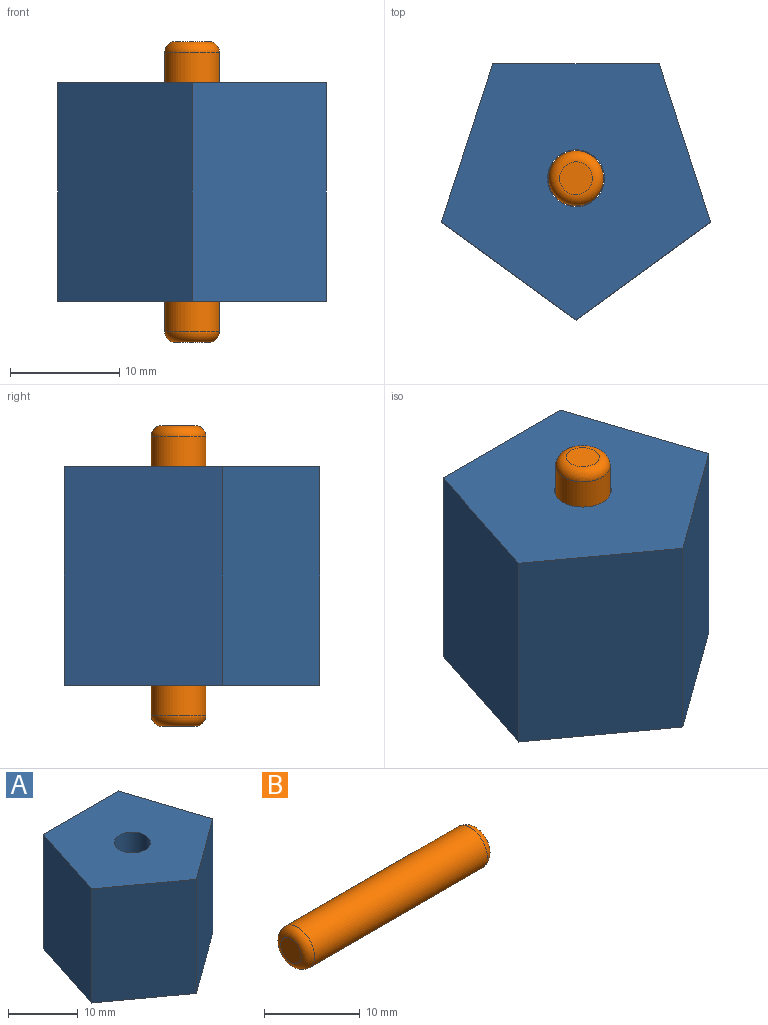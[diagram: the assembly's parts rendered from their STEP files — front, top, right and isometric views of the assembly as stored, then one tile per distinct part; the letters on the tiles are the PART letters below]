
ASSEMBLY  parts=2 mates=1
PART A: 8 faces, bbox 24.6x23.4x20 mm
  f0: plane 20x12.29mm, normal (0.59,-0.81,0), area 303.9mm2, adj f1,f5,f6,f7
  f1: plane 20x14.45mm, normal (0.95,0.31,0), area 303.9mm2, adj f0,f2,f6,f7
  f2: plane 20x15.19mm, normal (0,1,0), area 303.9mm2, adj f1,f3,f6,f7
  f3: plane 20x14.45mm, normal (-0.95,0.31,0), area 303.9mm2, adj f2,f5,f6,f7
  f4: cylinder r=2.6mm len=20mm, axis (0,0,-1), area 326.7mm2, adj f6,f7
  f5: plane 20x12.29mm, normal (-0.59,-0.81,0), area 303.9mm2, adj f0,f3,f6,f7
  f6: plane 24.59x23.38mm, normal (0,0,1), area 376mm2, adj f0,f1,f2,f3,f4,f5
  f7: plane 24.59x23.38mm, normal (0,0,-1), area 376mm2, adj f0,f1,f2,f3,f4,f5
PART B: 5 faces, bbox 27.5x5.4x5.4 mm
  f0: cylinder r=2.5mm len=25.5mm, axis (-1,0,0), area 400.6mm2, adj f3,f4
  f1: plane 3x3mm, normal (1,0,0), area 7.1mm2, adj f4
  f2: plane 3x3mm, normal (-1,0,0), area 7.1mm2, adj f3
  f3: torus R=1.5mm, axis (1,0,0), area 21.1mm2, adj f0,f2
  f4: torus R=1.5mm, axis (1,0,0), area 21.1mm2, adj f0,f1
PLACE A t=(0.02,4.9,-4.52)mm
PLACE B rot(axis=(0,-1,0),90deg) t=(0.02,4.9,-8.27)mm
MATE fastened B.f0 <-> A.f4  axis (0,0,-1) through (0.02,4.9,5.48)mm
